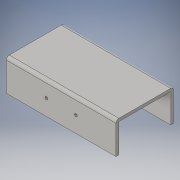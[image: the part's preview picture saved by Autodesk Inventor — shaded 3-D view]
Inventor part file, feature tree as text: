
AUTODESK INVENTOR PART (.ipt)
format: ipt  version: 2016 (Build 200138000, 138)  size: 130,560 bytes
history: native  units: in
note: dims shown in document units (in); Inventor stores cm internally (conversion verified against a paired STEP export)
features: sketch x4, extrude x3, fillet x2, hole x1
ambient origin geometry x8: Origin, YZ Plane, XZ Plane, XY Plane, X Axis, Y Axis, Z Axis, Center Point
bodies: Solid1 (feature_tree)
feature tree (10):
  extrude  "Extrusion1"  Depth=2.5in
  extrude  "Extrusion2"  Depth=1.25in
  extrude  "Extrusion4"  Depth=0.125in TaperAngle=0.0deg
  fillet  "Fillet1"  Radius=0.125in
  fillet  "Fillet2"  Radius=0.125in
  hole  "Hole1"  [1 undecoded]
  sketch  "Sketch1"  dims[d0=4.75in d1=2.5in]
  sketch  "Sketch2"  dims[d2=0.125in d3=0.0in d4=1.25in]
  sketch  "Sketch4"  dims[d5=0.125in d6=0.0in d9=0.125in d10=0.0in d11=0.125in d12=0.125in]
  sketch  "Sketch5"  dims[d14=1.28in d15=1.375in d16=0.6875in d17=0.6875in d18=4.75in d20=0.64in d21=0.6875in d22=2.375in d23=0.64in d24=0.1206in d25=0.75in d26=0.375in d27=0.25in d28=0.5635in d29=1.0in d30=0.8108in]
note: 1 required parameter value undecoded (feature->parameter linkage not recoverable at this tier; creation-order binding heuristic only, values carry confidence <= 0.55)
